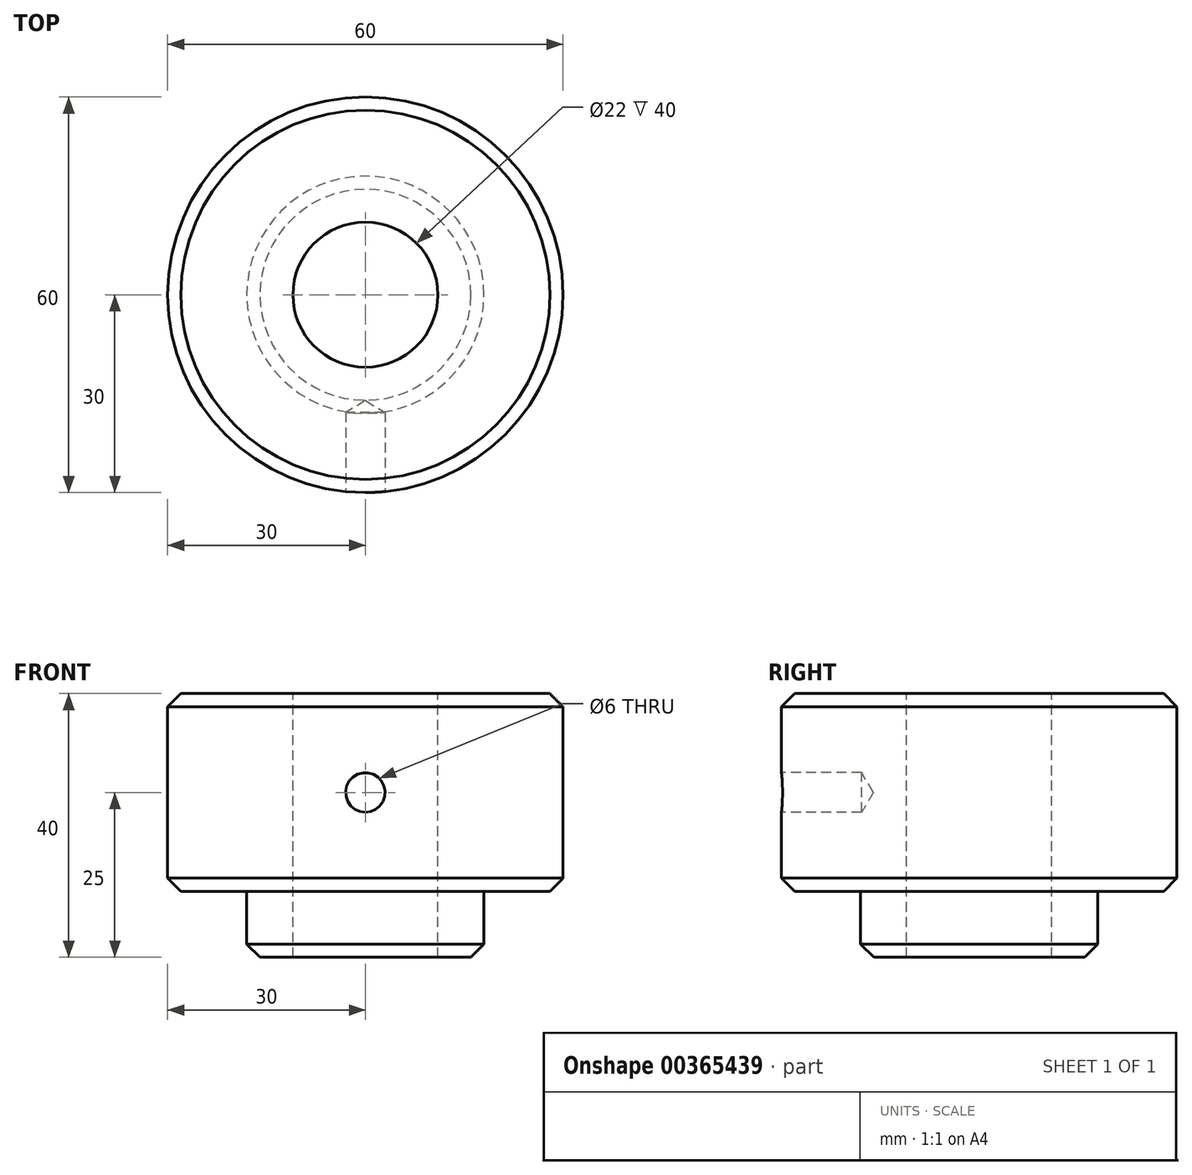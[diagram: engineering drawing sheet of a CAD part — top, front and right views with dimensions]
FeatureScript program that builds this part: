
annotation { "Feature Type Name" : "Feature", "Feature Type Description" : "" }
export const myFeature = defineFeature(function(context is Context, id is Id, definition is map)
    precondition{}
    {
        {
            var Q0;
            Q0=qCreatedBy(makeId("Front.planeOp"),FACE);
            var sketch = newSketch(context, id + "F0", { "sketchPlane" : qUnion([Q0])});
            skLineSegment(sketch, "E0", {"start": v(11, 30) * mm, "end": v(11, -10) * mm});
            skLineSegment(sketch, "E1", {"start": v(11, -10) * mm, "end": v(18, -10) * mm});
            skLineSegment(sketch, "E2", {"start": v(18, -10) * mm, "end": v(18, 0) * mm});
            skLineSegment(sketch, "E3", {"start": v(18, 0) * mm, "end": v(30, 0) * mm});
            skLineSegment(sketch, "E4", {"start": v(30, 0) * mm, "end": v(30, 30) * mm});
            skLineSegment(sketch, "E5", {"start": v(11, 30) * mm, "end": v(30, 30) * mm});
            skLineSegment(sketch, "E6", {"start": v(0, 64.47) * mm, "end": v(0, -49.43) * mm, "construction": true});
            skSolve(sketch);
        }
        {
            var Q0;
            Q0 = qSketchRegion(id + "F0", true);
            var Q1;
            Q1=sQuery(id+"F0.wireOp",EDGE,"E6");
            revolve(context, id + "F1", {"entities" : qUnion([Q0]), "axis" : qUnion([Q1]), "revolveType" : RevolveType.FULL});
        }
        {
            var Q0;
            Q0=makeQuery(id+"F1.opRevolve","SWEPT_EDGE",EDGE,{"disambiguationData":[OSD([sQuery(id+"F0.wireOp",EDGE,"E4"),sQuery(id+"F0.wireOp",EDGE,"E5")])]});
            var Q1;
            Q1=makeQuery(id+"F1.opRevolve","SWEPT_EDGE",EDGE,{"disambiguationData":[OSD([sQuery(id+"F0.wireOp",EDGE,"E3"),sQuery(id+"F0.wireOp",EDGE,"E4")])]});
            var Q2;
            Q2=makeQuery(id+"F1.opRevolve","SWEPT_EDGE",EDGE,{"disambiguationData":[OSD([sQuery(id+"F0.wireOp",EDGE,"E1"),sQuery(id+"F0.wireOp",EDGE,"E2")])]});
            chamfer(context, id + "F2", {"entities" : qUnion([Q0, Q1, Q2]), "width" : 2 * mm, "tangentPropagation" : true});
        }
        {
            var Q0;
            Q0=qCreatedBy(makeId("Front.planeOp"),FACE);
            cPlane(context, id + "F3", {"entities" : qUnion([Q0]), "cplaneType" : CPlaneType.OFFSET, "offset" : 30 * mm, "width" : 150 * mm, "height" : 150 * mm});
        }
        {
            var Q0;
            Q0=qCreatedBy(id+"F3.planeOp",FACE);
            var sketch = newSketch(context, id + "F4", { "sketchPlane" : qUnion([Q0])});
            skPoint(sketch, "E7", {"position": v(0, 15) * mm});
            skSolve(sketch);
        }
        {
            var Q0;
            Q0=sQuery(id+"F4.wireOp",VERTEX,"E7");
            var Q1;
            Q1=makeQuery(id+"F1.opRevolve","SWEPT_BODY",BODY,{"disambiguationData":[OSD([sQuery(id+"F0.wireOp",EDGE,"E0"),sQuery(id+"F0.wireOp",EDGE,"E1"),sQuery(id+"F0.wireOp",EDGE,"E2"),sQuery(id+"F0.wireOp",EDGE,"E3"),sQuery(id+"F0.wireOp",EDGE,"E4"),sQuery(id+"F0.wireOp",EDGE,"E5")])]});
            hole(context, id + "F5", {"style" : HoleStyle.SIMPLE, "endStyle" : HoleEndStyle.BLIND, "holeDiameter" : 6 * mm, "holeDepth" : 12 * mm, "isTappedThrough" : true, "tappedDepth" : 12 * mm, "tapClearance" : 3, "locations" : qUnion([Q0]), "scope" : qUnion([Q1])});
        }
    });
